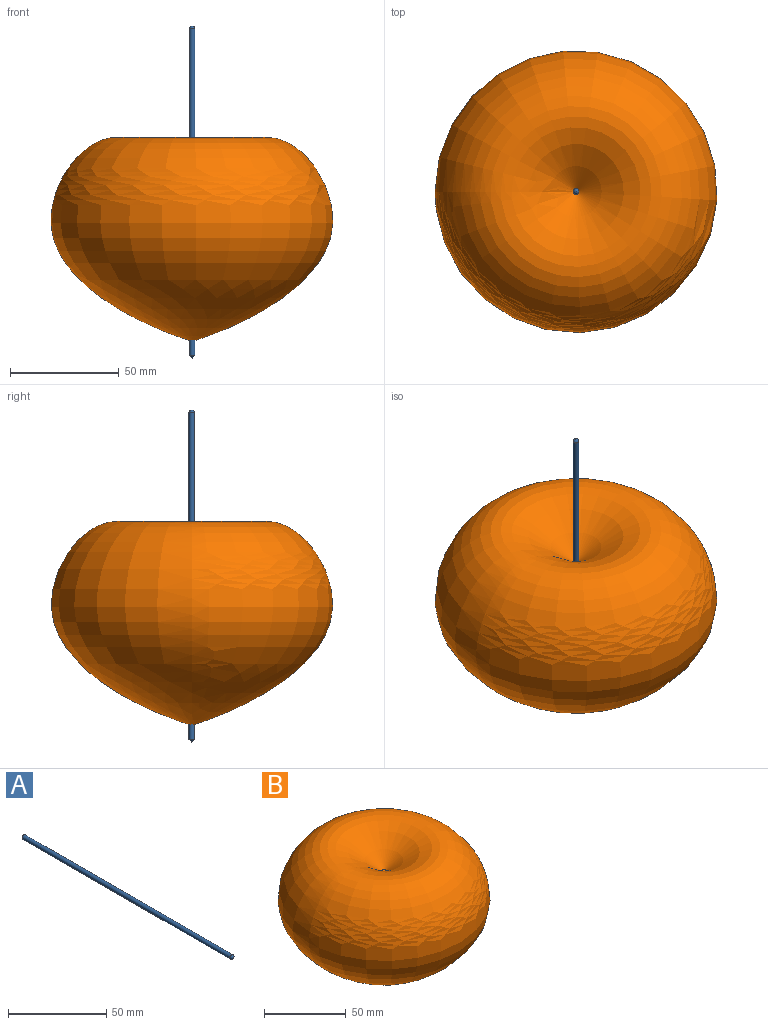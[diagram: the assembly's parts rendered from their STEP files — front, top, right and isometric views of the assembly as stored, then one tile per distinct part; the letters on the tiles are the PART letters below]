
ASSEMBLY  parts=2 mates=1
PART A: 3 faces, bbox 2.5x152.4x2.5 mm
  f0: cylinder r=1.27mm len=149.86mm, axis (0,1,0), area 1195.8mm2, adj f1,f2
  f1: sphere r=1.27mm, area 10.1mm2, adj f0
  f2: cone r=1.27mm half-angle=45deg, axis (0,-1,0), area 7.2mm2, adj f0
PART B: 2 faces, bbox 129.5x129.5x93.6 mm
  f0: revolved ~129.5x129.5mm, area 43886.3mm2, adj f1
  f1: plane 2.54x2.54mm, normal (0,0,1), area 5.1mm2, adj f0
PLACE A rot(axis=(-1,0,0),90deg) t=(0,0,-7.62)mm
PLACE B at identity
MATE fastened A.f0 <-> B.f0  axis (0,0,1) through (0,0,-6.35)mm
